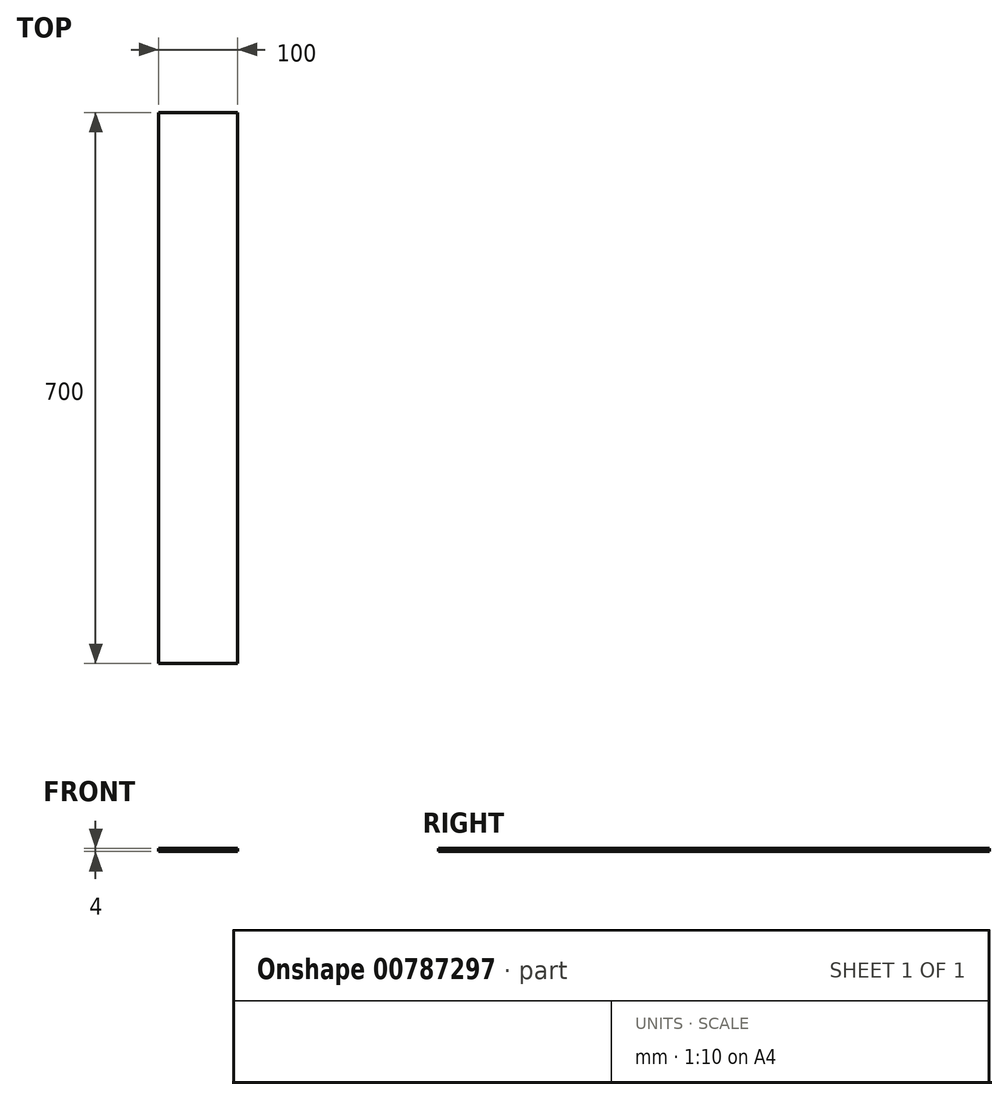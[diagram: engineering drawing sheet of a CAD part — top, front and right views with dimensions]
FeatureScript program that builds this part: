
annotation { "Feature Type Name" : "Feature", "Feature Type Description" : "" }
export const myFeature = defineFeature(function(context is Context, id is Id, definition is map)
    precondition{}
    {
        {
            var Q0;
            Q0=qCreatedBy(makeId("Front.planeOp"),FACE);
            var sketch = newSketch(context, id + "F0", { "sketchPlane" : qUnion([Q0])});
            skLineSegment(sketch, "E0.bottom", {"start": v(50, 2) * mm, "end": v(-50, 2) * mm});
            skLineSegment(sketch, "E0.top", {"start": v(50, -2) * mm, "end": v(-50, -2) * mm});
            skLineSegment(sketch, "E0.left", {"start": v(50, 2) * mm, "end": v(50, -2) * mm});
            skLineSegment(sketch, "E0.right", {"start": v(-50, 2) * mm, "end": v(-50, -2) * mm});
            skPoint(sketch, "E0.middle", {"position": v(0, 0) * mm});
            skSolve(sketch);
        }
        {
            var Q0;
            Q0 = qSketchRegion(id + "F0", true);
            extrude(context, id + "F1", {"entities" : qUnion([Q0]), "depth" : 700 * mm, "offsetDistance" : 25 * mm});
        }
    });
